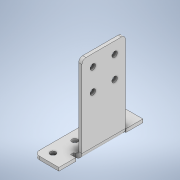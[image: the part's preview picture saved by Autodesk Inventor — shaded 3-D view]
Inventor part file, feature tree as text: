
AUTODESK INVENTOR PART (.ipt)
format: ipt  version: 2020 (Build 240168000, 168)  size: 243,200 bytes
history: native  units: mm
features: sketch x4, sheet_metal_op x2, hole x2, chamfer x2, other x2
ambient origin geometry x8: Origin, YZ Plane, XZ Plane, XY Plane, X Axis, Y Axis, Z Axis, Center Point
bodies: Solid1 (feature_tree)
feature tree (12):
  sheet_metal_op  "Face1"
  sheet_metal_op  "Fold1"
  hole  "Hole1"  [1 undecoded]
  hole  "Hole2"  [1 undecoded]
  chamfer  "Corner Round1"
  chamfer  "Corner Round2"
  sketch  "Sketch2"  dims[d7=3.0mm d8=3.0mm]
  other  "Plate1"
  sketch  "Sketch3"  dims[d9=1.5mm d10=6.0mm]
  sketch  "Sketch4"  dims[d11=3.0mm]
  sketch  "Sketch5"  dims[d12=90.0deg d13=3.0mm d14=5.1mm d15=5.1mm d16=5.1mm d17=5.1mm d18=14.0mm d19=14.0mm d20=14.0mm d21=14.0mm d22=10.0mm d23=10.0mm d24=30.0mm d25=30.0mm d26=5.1mm d27=6.0mm d28=4.0mm d29=2.0mm d30=90.0deg d31=3.0mm d32=20.594885mm d33=5.1mm d34=5.1mm d35=5.1mm d36=5.1mm d37=70.0mm d38=10.0mm d39=10.0mm d40=10.0mm d41=10.0mm d42=70.0mm d43=50.0mm d44=50.0mm d45=5.1mm d46=6.0mm d47=4.0mm d48=2.0mm d49=90.0deg d50=3.0mm d51=20.594885mm d52=3.7mm d53=4.64mm d54=22.58mm d55=77.15mm d56=18.575mm d57=18.575mm d58=20.0mm d59=20.0mm d60=78.0mm]
  other  "Definition1"
note: 2 required parameter values undecoded (feature->parameter linkage not recoverable at this tier; creation-order binding heuristic only, values carry confidence <= 0.55)
